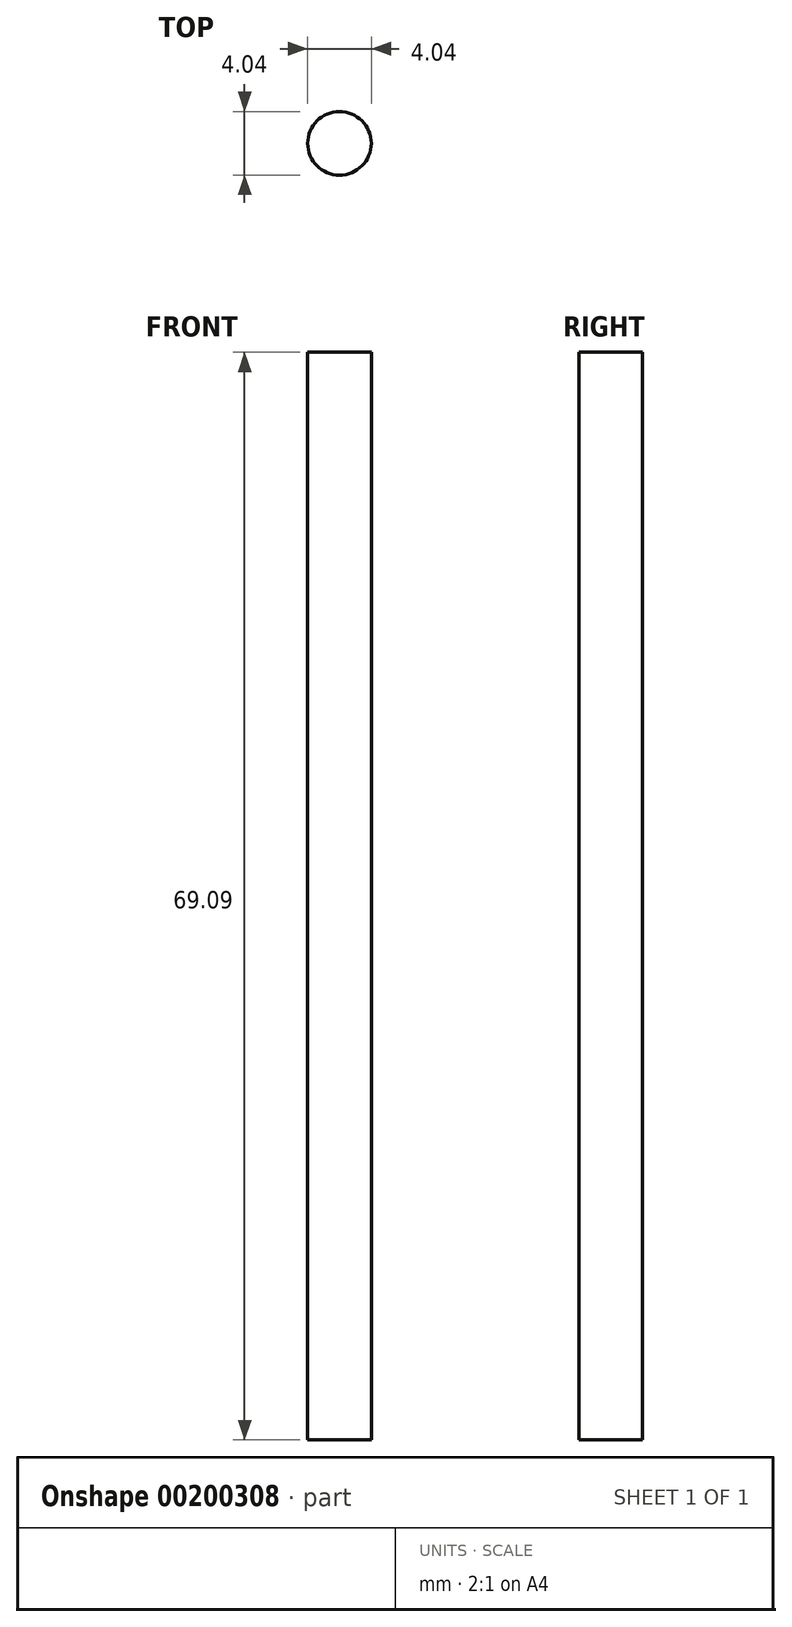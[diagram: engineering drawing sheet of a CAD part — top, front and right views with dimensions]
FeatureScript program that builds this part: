
annotation { "Feature Type Name" : "Feature", "Feature Type Description" : "" }
export const myFeature = defineFeature(function(context is Context, id is Id, definition is map)
    precondition{}
    {
        {
            var Q0;
            Q0=qCreatedBy(makeId("Top.planeOp"),FACE);
            var sketch = newSketch(context, id + "F0", { "sketchPlane" : qUnion([Q0])});
            skCircle(sketch, "E0", {"center": v(0, 0) * mm, "radius": 2.02 * mm});
            skSolve(sketch);
        }
        {
            var Q0;
            Q0=makeQuery(id+"F0.imprint","IMPRINT",FACE,{"disambiguationData":[TD([[makeQuery(id+"F0.imprint","IMPRINT",EDGE,{"derivedFrom":sQuery(id+"F0.wireOp",EDGE,"E0")}),1.0]])]});
            extrude(context, id + "F1", {"entities" : qUnion([Q0]), "depth" : 69.1 * mm});
        }
    });
